# Revit family: 307_Cim3723B-_
name_source: partatom
category: Pipe Accessories
units: mm (PartAtom-declared; Revit-internal decimal feet)

## family parameters
Always vertical = Yes
Cut with Voids When Loaded = No
Part Type = Breaks Into
Round Connector Dimension = Use Diameter
Shared = No
Work Plane-Based = No

## types (9) — shared parameters
CAT0 = Yes
D2 = 15 mm  [stored 0.0492126 ft]
Description = METERING STATION - PN 16 - STAINLESS STEEL - FLANGED END
L = 20 mm  [stored 0.0656168 ft]
L2D = 20 mm  [stored 0.0656168 ft]
L2D_Min = 3048 mm  [stored 10 ft]
LL1 = 10 mm  [stored 0.0328084 ft]
Manufacturer = Cimberio
QmdConnectorList = 301;D;302;D
URL = www.cimberio.it
magiPartTypeId = 307
magiProductFamilyId = Cim3723B-*
zero-valued in all types: MC_Default_elevation

## per-type parameters (varying)
| type | D | D1 | H | W2D |
| Cim3723B-50 | 50 mm | 108 mm  [stored 0.354331 ft] | 136 mm  [stored 0.446194 ft] | 50 mm  [stored 0.164042 ft] |
| Cim3723B-300 | 300 mm | 385 mm  [stored 1.26312 ft] | 304 mm  [stored 0.997375 ft] | 300 mm  [stored 0.984252 ft] |
| Cim3723B-250 | 50 mm | 108 mm  [stored 0.354331 ft] | 136 mm  [stored 0.446194 ft] | 250 mm |
| Cim3723B-200 | 200 mm | 275 mm  [stored 0.902231 ft] | 219 mm  [stored 0.718504 ft] | 200 mm  [stored 0.656168 ft] |
| Cim3723B-150 | 150 mm | 220 mm  [stored 0.721785 ft] | 192 mm  [stored 0.629921 ft] | 150 mm  [stored 0.492126 ft] |
| Cim3723B-125 | 125 mm | 194 mm  [stored 0.636483 ft] | 179 mm  [stored 0.58727 ft] | 125 mm  [stored 0.410105 ft] |
| Cim3723B-100 | 100 mm | 164 mm  [stored 0.538058 ft] | 164 mm  [stored 0.538058 ft] | 100 mm  [stored 0.328084 ft] |
| Cim3723B-80 | 80 mm | 144 mm  [stored 0.472441 ft] | 154 mm  [stored 0.505249 ft] | 80 mm  [stored 0.262467 ft] |
| Cim3723B-65 | 65 mm | 125 mm  [stored 0.410105 ft] | 145 mm  [stored 0.475722 ft] | 65 mm  [stored 0.213255 ft] |

note: column(s) folded — value = type name in every type: magiProductCode, magiProductId

note: [stored X ft] marks values corroborated as IEEE doubles in the binary element streams (Revit-internal decimal feet)

## geometry (parser evidence)
native form markers: Sweep x2
no freeform markers — native parametric forms only
